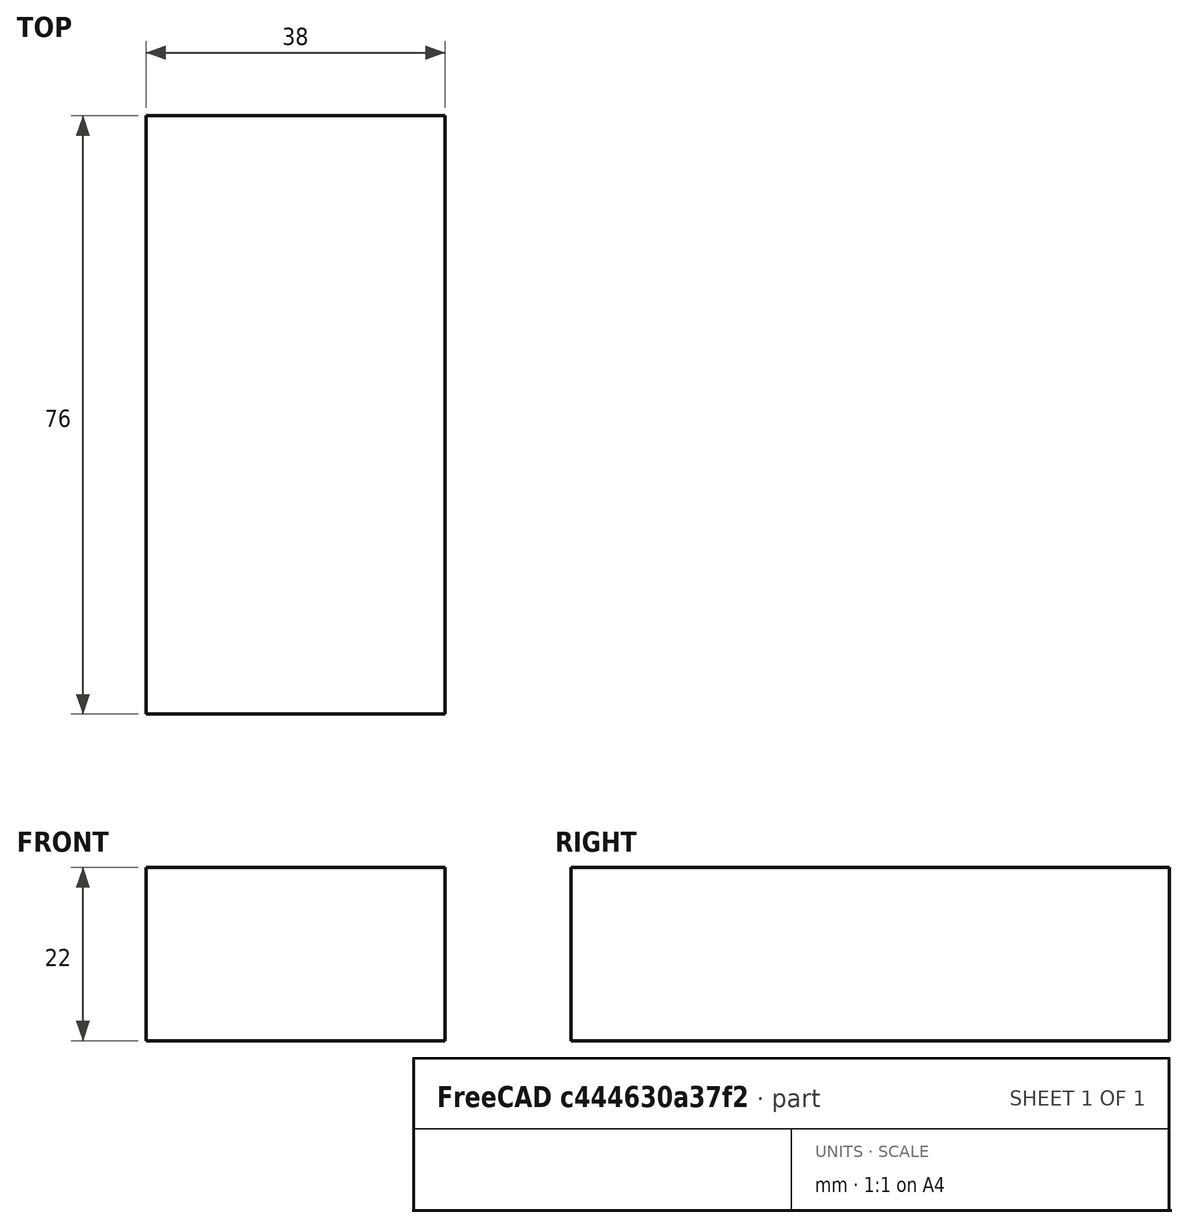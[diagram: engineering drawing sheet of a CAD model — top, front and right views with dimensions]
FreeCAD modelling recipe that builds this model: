
FCSTD DOCUMENT  (FreeCAD 1.0R39319 (Git))
Label: battery_pack
License: All rights reserved
LicenseURL: http://en.wikipedia.org/wiki/All_rights_reserved
objects: Spreadsheet::Sheet×1, Sketcher::SketchObject×1, PartDesign::Pad×1, PartDesign::Body×1
note: 6 computed .brp shape members not serialized (recipe doc carries the construction recipe); baked Part::Feature solids carry a one-line shape summary decoded from their .brp

FEATURE [Spreadsheet::Sheet] Spreadsheet
  cells = A2='width; B2(width)=38; A3='length; B3(length)=76; A4='height; B4(height)=22
FEATURE [Sketcher::SketchObject] Sketch
  ArcFitTolerance = 1e-06
  AttachmentSupport = -> [XY_Plane]
  FullyConstrained = true
  MakeInternals = false
  MapMode = 5
  expr: Constraints[8] = Spreadsheet.width
  expr: Constraints[9] = Spreadsheet.length
  sketch-geometry (4):
    g0: LineSegment StartX=10 StartY=46 StartZ=0 EndX=10 EndY=-30 EndZ=0
    g1: LineSegment StartX=10 StartY=-30 StartZ=0 EndX=48 EndY=-30 EndZ=0
    g2: LineSegment StartX=48 StartY=-30 StartZ=0 EndX=48 EndY=46 EndZ=0
    g3: LineSegment StartX=48 StartY=46 StartZ=0 EndX=10 EndY=46 EndZ=0
  constraints (12):
    c: Coincident(g0,g1)
    c: Coincident(g1,g2)
    c: Coincident(g2,g3)
    c: Coincident(g3,g0)
    c: Vertical(g0)
    c: Vertical(g2)
    c: Horizontal(g1)
    c: Horizontal(g3)
    c: DistanceX(g0,g1) = 38
    c: DistanceY(g1,g2) = 76
    c: DistanceY(g0,g-1) = 30
    c: DistanceX(g-1,g0) = 10
FEATURE [PartDesign::Pad] Pad
  Direction = (0,0,1)
  Length = 22
  Length2 = 10
  Profile = -> Sketch
  ReferenceAxis = -> Sketch [N_Axis]
  Suppressed = false
  Type = 0
  expr: Length = Spreadsheet.height
FEATURE [PartDesign::Body] Body
  AllowCompound = false
  Group = -> [Sketch,Pad]
  Origin = -> Origin
  Tip = -> Pad
